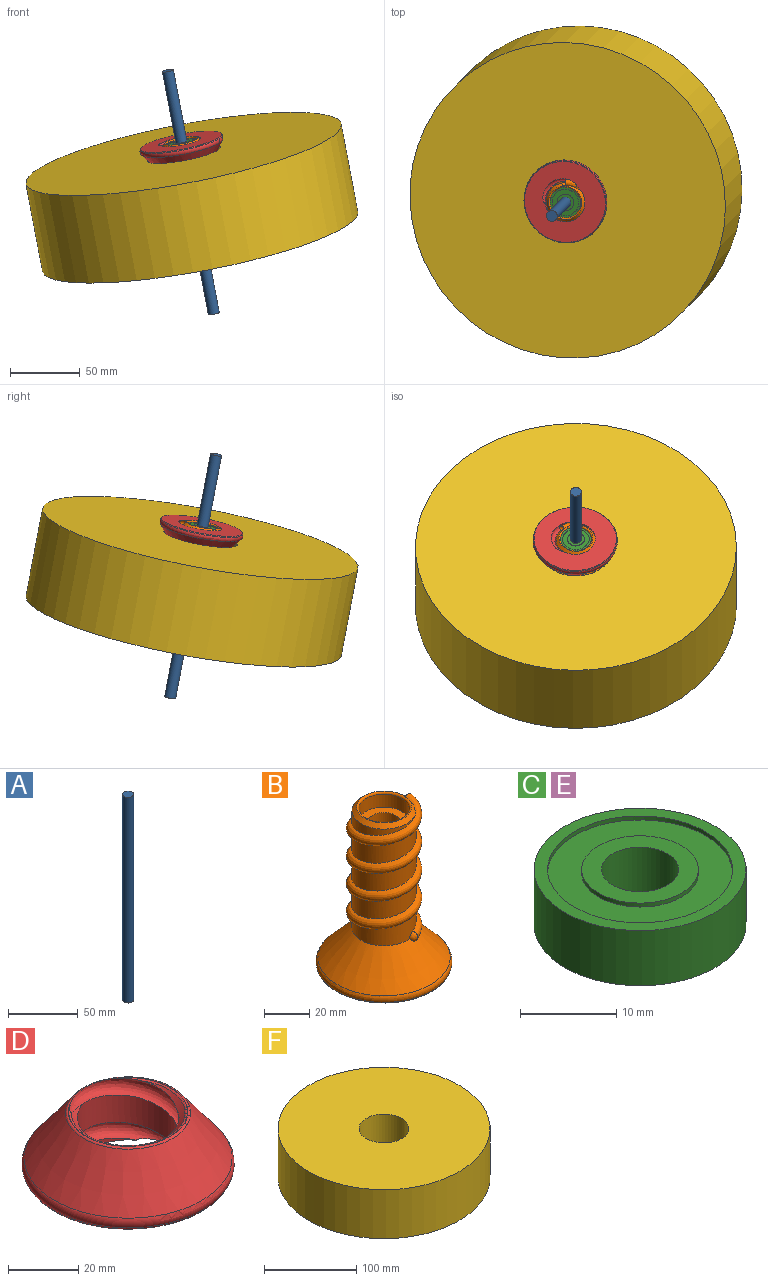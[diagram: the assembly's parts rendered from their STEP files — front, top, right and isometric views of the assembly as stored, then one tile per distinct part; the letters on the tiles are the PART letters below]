
ASSEMBLY  parts=6 mates=7
PART A: 3 faces, bbox 8x8x180 mm
  f0: cylinder r=4mm len=180mm, axis (0,0,-1), area 4523.9mm2, adj f1,f2
  f1: plane 8x8mm, normal (0,0,1), area 50.3mm2, adj f0
  f2: plane 8x8mm, normal (0,0,-1), area 50.3mm2, adj f0
PART B: 17 faces, bbox 64.8x64.8x86 mm
  f0: cylinder r=14.15mm len=63mm, axis (0,0,-1), area 3752.9mm2, adj f1,f8,f9,f15,f16
  f1: cone r=32.5mm half-angle=42.5deg, axis (0,0,-1), area 2991.4mm2, adj f0,f2,f15,f16
  f2: torus R=26.94mm, axis (0,0,-1), area 648.3mm2, adj f1,f3
  f3: cone r=30.47mm half-angle=23.7deg, axis (0,0,1), area 84.9mm2, adj f2,f4
  f4: plane 59x59mm, normal (0,0,-1), area 2270.2mm2, adj f3,f5
  f5: cone r=11.15mm half-angle=45deg, axis (0,0,-1), area 103.5mm2, adj f4,f6
  f6: cylinder r=11.15mm len=22.3mm, axis (0,0,-1), area 490.4mm2, adj f5,f7
  f7: plane 22.3x22.3mm, normal (0,0,-1), area 390.6mm2, adj f6
  f8: sphere r=2.5mm, area 49mm2, adj f0,f9,f15
  f9: cone r=12.15mm half-angle=45deg, axis (0,0,-1), area 211.8mm2, adj f0,f8,f10,f15
  f10: torus R=12.15mm, axis (0,0,1), area 113.6mm2, adj f9,f11
  f11: cylinder r=11.15mm len=22.3mm, axis (0,0,1), area 490.4mm2, adj f10,f12
  f12: plane 22.3x22.3mm, normal (0,0,1), area 236.6mm2, adj f11,f13
  f13: cylinder r=7mm len=68.7mm, axis (0,0,-1), area 3021.6mm2, adj f12,f14
  f14: plane 14x14mm, normal (0,0,1), area 153.9mm2, adj f13
  f15: bspline ~67.98x33.26mm, area 3278.6mm2, adj f0,f1,f8,f9,f16
  f16: revolved ~4.94x4.34mm, area 16.2mm2, adj f0,f1,f15
PART C: 12 faces, bbox 22x22x7 mm
  f0: plane 12.1x12.1mm, normal (0,0,-1), area 64.7mm2, adj f2,f9
  f1: plane 12.1x12.1mm, normal (0,0,1), area 64.7mm2, adj f2,f6
  f2: cylinder r=4mm len=8mm, axis (0,0,-1), area 175.9mm2, adj f0,f1
  f3: cylinder r=11mm len=22mm, axis (0,0,-1), area 483.8mm2, adj f4,f5
  f4: plane 22x22mm, normal (0,0,1), area 90.6mm2, adj f3,f7
  f5: plane 22x22mm, normal (0,0,-1), area 90.6mm2, adj f3,f10
  f6: cylinder r=6.05mm len=12.1mm, axis (0,0,1), area 19mm2, adj f1,f8
  f7: cylinder r=9.6mm len=19.2mm, axis (0,0,1), area 30.2mm2, adj f4,f8
  f8: plane 19.2x19.2mm, normal (0,0,1), area 174.5mm2, adj f6,f7
  f9: cylinder r=6.05mm len=12.1mm, axis (0,0,-1), area 19mm2, adj f0,f11
  f10: cylinder r=9.6mm len=19.2mm, axis (0,0,-1), area 30.2mm2, adj f5,f11
  f11: plane 19.2x19.2mm, normal (0,0,-1), area 174.5mm2, adj f9,f10
PART D: 10 faces, bbox 65.4x65.4x37.3 mm
  f0: plane 59x59mm, normal (0,0,-1), area 1995.4mm2, adj f3,f4,f8
  f1: plane 34x32.1mm, normal (0,0,1), area 7.6mm2, adj f4,f6,f7
  f2: cone r=32.5mm half-angle=36.9deg, axis (0,0,-1), area 2924.7mm2, adj f7,f9
  f3: cylinder r=14.5mm len=29mm, axis (0,0,1), area 1038.6mm2, adj f0,f4,f5
  f4: bspline ~37.25x34.5mm, area 1153.1mm2, adj f0,f1,f3,f5,f6,f7
  f5: cone r=14.5mm half-angle=45deg, axis (0,0,1), area 156.8mm2, adj f3,f4,f6
  f6: torus R=16.91mm, axis (0,0,1), area 62.1mm2, adj f1,f4,f5
  f7: torus R=17mm, axis (0,0,1), area 98.8mm2, adj f1,f2,f4
  f8: cone r=30.7mm half-angle=26.6deg, axis (0,0,1), area 154.7mm2, adj f0,f9
  f9: torus R=27.19mm, axis (0,0,-1), area 626.6mm2, adj f2,f8
PART E: same geometry as C
PART F: 4 faces, bbox 230x230x65 mm
  f0: cylinder r=27mm len=65mm, axis (0,0,-1), area 11027mm2, adj f2,f3
  f1: cylinder r=115mm len=230mm, axis (0,0,-1), area 46966.8mm2, adj f2,f3
  f2: plane 230x230mm, normal (0,0,1), area 39257.3mm2, adj f0,f1
  f3: plane 230x230mm, normal (0,0,-1), area 39257.3mm2, adj f0,f1
PLACE A rot(axis=(0,-0.18,0.98),91deg) t=(-89.21,33.73,-49.35)mm
PLACE B rot(axis=(0,-0.18,0.98),91deg) t=(-97.09,25.85,-7.76)mm
PLACE C rot(axis=(0,-0.18,0.98),91deg) t=(-111.18,11.76,66.62)mm
PLACE D rot(axis=(-0.7,-0.7,-0.13),180deg) t=(-114.04,84.61,87.33)mm
PLACE E rot(axis=(0,-0.18,0.98),91deg) t=(-97.27,25.66,-6.79)mm
PLACE F rot(axis=(0,-0.18,0.98),91deg) t=(-98.95,23.98,2.09)mm
MATE slider A.f0 <-> B.f0  axis (0.18,0.18,-0.97) through (-105.68,17.26,37.59)mm
MATE slider D.f0 <-> B.f0  axis (-0.18,-0.18,0.97) through (-112.5,10.44,73.57)mm
MATE planar C.f3 <-> B.f0  axis (0.18,0.18,-0.97) through (-111.18,11.76,66.62)mm
MATE slider E.f6 <-> B.f0  axis (0.18,0.18,-0.97) through (-97.27,25.66,-6.79)mm
MATE planar E.f3 <-> B.f0  axis (-0.18,-0.18,0.97) through (-98.55,24.38,-0.03)mm
MATE slider C.f6 <-> B.f0  axis (-0.18,-0.18,0.97) through (-112.37,10.57,72.9)mm
MATE slider F.f0 <-> B.f0  axis (0.18,0.18,-0.97) through (-110.85,12.09,64.87)mm
